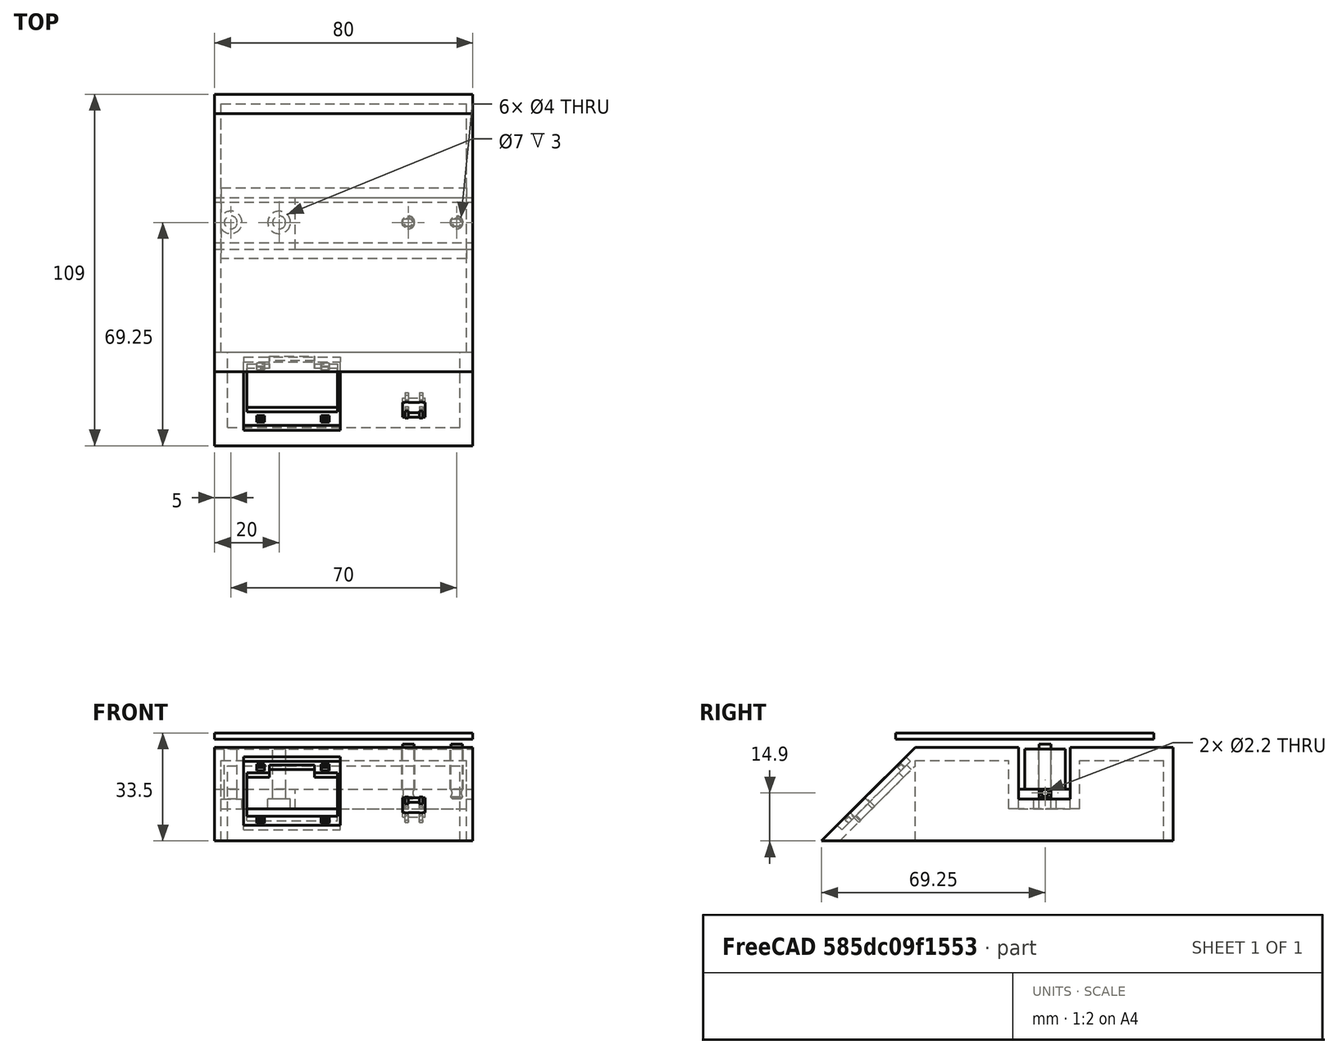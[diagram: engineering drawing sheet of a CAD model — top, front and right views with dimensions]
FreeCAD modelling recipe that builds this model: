
FCSTD DOCUMENT  (FreeCAD 0.19R24291 (Git))
Label: Scale
License: All rights reserved
LicenseURL: http://en.wikipedia.org/wiki/All_rights_reserved
objects: Part::Box×19, Part::Cylinder×11, Part::Cut×5, Part::MultiFuse×4, Part::Compound×3, Part::FeaturePython×3, Part::Chamfer×2, Mesh::Feature×1, Part::Thickness×1, Part::MultiCommon×1
note: 49 computed .brp shape members not serialized (recipe doc carries the construction recipe); baked Part::Feature solids carry a one-line shape summary decoded from their .brp

FEATURE [Part::Box] Box  label="Eje001"
  AttacherType = Attacher::AttachEngine3D
  Height = 12.5
  Length = 80
  Width = 12.5
FEATURE [Part::Cylinder] Cylinder
  Angle = 360
  AttacherType = Attacher::AttachEngine3D
  AttachmentOffset = pos=(5,6.25,-12.5) rot=(0,0,1;0rad)
  Height = 13
  MapMode = 5
  Placement = pos=(5,6.25,0) rot=(0,0,1;0rad)
  Radius = 2
  Support = -> [Box]
  expr: .AttachmentOffset.Base.y = Box.Width / 2
  expr: .AttachmentOffset.Base.z = -Box.Height
FEATURE [Part::Cylinder] Cylinder001
  Angle = 360
  AttacherType = Attacher::AttachEngine3D
  AttachmentOffset = pos=(20,6.25,-12.5) rot=(0,0,1;0rad)
  Height = 13
  MapMode = 5
  Placement = pos=(20,6.25,0) rot=(0,0,1;0rad)
  Radius = 2
  Support = -> [Box]
  expr: .AttachmentOffset.Base.y = Box.Width / 2
  expr: .AttachmentOffset.Base.z = -Box.Height
FEATURE [Part::Cylinder] Cylinder002
  Angle = 360
  AttacherType = Attacher::AttachEngine3D
  AttachmentOffset = pos=(75,6.25,-12.5) rot=(0,0,1;0rad)
  Height = 13
  MapMode = 5
  Placement = pos=(75,6.25,0) rot=(0,0,1;0rad)
  Radius = 2
  Support = -> [Box]
  expr: .AttachmentOffset.Base.y = Box.Width / 2
  expr: .AttachmentOffset.Base.z = -Box.Height
  expr: .AttachmentOffset.Base.x = Box.Length - 5mm
FEATURE [Part::Cylinder] Cylinder003
  Angle = 360
  AttacherType = Attacher::AttachEngine3D
  AttachmentOffset = pos=(60,6.25,-12.5) rot=(0,0,1;0rad)
  Height = 13
  MapMode = 5
  Placement = pos=(60,6.25,0) rot=(0,0,1;0rad)
  Radius = 2
  Support = -> [Box]
  expr: .AttachmentOffset.Base.y = Box.Width / 2
  expr: .AttachmentOffset.Base.z = -Box.Height
  expr: .AttachmentOffset.Base.x = Box.Length - 20mm
FEATURE [Part::Compound] Compound  label="AgujerosEje"
  Links = -> [Cylinder,Cylinder001,Cylinder002,Cylinder003]
FEATURE [Part::Cut] Cut  label="Eje"
  Base = -> Box
  Tool = -> Compound
FEATURE [Part::Cylinder] Cylinder004
  Angle = 360
  AttacherType = Attacher::AttachEngine3D
  AttachmentOffset = pos=(75,6.25,-12.5) rot=(0,0,1;0rad)
  Height = 17
  Placement = pos=(75,6.25,-3) rot=(0,0,1;0rad)
  Radius = 1.8
  Support = -> [Box]
  expr: .AttachmentOffset.Base.y = Box.Width / 2
  expr: .AttachmentOffset.Base.z = -Box.Height
  expr: .AttachmentOffset.Base.x = Box.Length - 5mm
FEATURE [Part::Cylinder] Cylinder005
  Angle = 360
  AttacherType = Attacher::AttachEngine3D
  AttachmentOffset = pos=(60,6.25,-12.5) rot=(0,0,1;0rad)
  Height = 17
  Placement = pos=(60,6.25,-3) rot=(0,0,1;0rad)
  Radius = 1.8
  Support = -> [Box]
  expr: .AttachmentOffset.Base.y = Box.Width / 2
  expr: .AttachmentOffset.Base.z = -Box.Height
  expr: .AttachmentOffset.Base.x = Box.Length - 20mm
FEATURE [Part::Compound] Compound001  label="PernosPlato001"
  Links = -> [Cylinder005,Cylinder004]
FEATURE [Part::Chamfer] Chamfer  label="PernosPlato002"
  Base = -> Compound001
  Edges = 2 edges r=0.5: [Edge3,Edge6]
FEATURE [Part::Cylinder] Cylinder006  label="OrificioTransversalPernos"
  Angle = 360
  AttacherType = Attacher::AttachEngine3D
  Height = 25
  Placement = pos=(55,6.25,-1.1) rot=(0,1,0;1.5708rad)
  Radius = 1.1
  expr: .Placement.Base.y = Box.Width / 2
  expr: .Placement.Base.x = Box.Length - Height
  expr: .Placement.Base.z = -Radius
FEATURE [Part::Cut] Cut001  label="PernosPlato"
  Base = -> Chamfer
  Tool = -> Cylinder006
FEATURE [Part::Box] Box001  label="Plato001"
  AttacherType = Attacher::AttachEngine3D
  Height = 2
  Length = 80
  Placement = pos=(0,-40,15.5) rot=(0,0,1;0rad)
  Width = 80
  expr: Length = <<Eje001>>.Length
  expr: Width = <<Eje001>>.Length
  expr: .Placement.Base.y = -Width / 2
  expr: .Placement.Base.z = <<Eje001>>.Height + 3mm
FEATURE [Part::Box] Box002  label="Soporte001"
  AttacherType = Attacher::AttachEngine3D
  Height = 6
  Length = 25
  Placement = pos=(0,-2,-6) rot=(0,0,1;0rad)
  Width = 16
FEATURE [Part::Compound] Compound003  label="Plato MAL"
  Links = -> [Box001,Cut001]
FEATURE [Mesh::Feature] BasculaPlato  label="Plato STL"
FEATURE [Part::Cylinder] Cylinder007
  Angle = 360
  AttacherType = Attacher::AttachEngine3D
  AttachmentOffset = pos=(20,6.25,-12.5) rot=(0,0,1;0rad)
  Height = 20
  MapMode = 5
  Placement = pos=(20,6.25,0) rot=(0,0,1;0rad)
  Radius = 2
  Support = -> [Box]
  expr: .AttachmentOffset.Base.y = Box.Width / 2
  expr: .AttachmentOffset.Base.z = -Box.Height
FEATURE [Part::Cylinder] Cylinder008
  Angle = 360
  AttacherType = Attacher::AttachEngine3D
  AttachmentOffset = pos=(5,6.25,-12.5) rot=(0,0,1;0rad)
  Height = 20
  MapMode = 5
  Placement = pos=(5,6.25,0) rot=(0,0,1;0rad)
  Radius = 2
  Support = -> [Box]
  expr: .AttachmentOffset.Base.y = Box.Width / 2
  expr: .AttachmentOffset.Base.z = -Box.Height
FEATURE [Part::Cylinder] Cylinder009
  Angle = 360
  AttacherType = Attacher::AttachEngine3D
  AttachmentOffset = pos=(5,6.25,-15.5) rot=(0,0,1;0rad)
  Height = 6
  MapMode = 5
  Placement = pos=(5,6.25,-3) rot=(0,0,1;0rad)
  Radius = 3.5
  Support = -> [Box]
  expr: .AttachmentOffset.Base.y = Box.Width / 2
  expr: .AttachmentOffset.Base.z = -Box.Height - 3mm
FEATURE [Part::Cylinder] Cylinder010
  Angle = 360
  AttacherType = Attacher::AttachEngine3D
  AttachmentOffset = pos=(20,6.25,-15.5) rot=(0,0,1;0rad)
  Height = 6
  MapMode = 5
  Placement = pos=(20,6.25,-3) rot=(0,0,1;0rad)
  Radius = 3.5
  Support = -> [Box]
  expr: .AttachmentOffset.Base.y = Box.Width / 2
  expr: .AttachmentOffset.Base.z = -Box.Height - 3mm
FEATURE [Part::MultiFuse] Fusion
  Placement = pos=(0,0,-6) rot=(0,0,1;0rad)
  Shapes = -> [Cylinder008,Cylinder007,Cylinder009,Cylinder010]
FEATURE [Part::Cut] Cut002
  Base = -> Box002
  Tool = -> Fusion
FEATURE [Part::Box] Box003  label="Soporte002"
  AttacherType = Attacher::AttachEngine3D
  Height = 4
  Length = 80
  Placement = pos=(0,-34,9) rot=(0,0,1;0rad)
  Width = 32
FEATURE [Part::Box] Box004  label="Soporte003"
  AttacherType = Attacher::AttachEngine3D
  Height = 4
  Length = 80
  Placement = pos=(0,14,9) rot=(0,0,1;0rad)
  Width = 32
FEATURE [Part::Box] Box005  label="Soporte004"
  AttacherType = Attacher::AttachEngine3D
  Height = 18
  Length = 80
  Placement = pos=(0,-5,-6) rot=(0,0,1;0rad)
  Width = 3
FEATURE [Part::Box] Box006  label="Soporte005"
  AttacherType = Attacher::AttachEngine3D
  Height = 18
  Length = 80
  Placement = pos=(0,14,-6) rot=(0,0,1;0rad)
  Width = 3
FEATURE [Part::Box] Box008  label="Fondo001"
  AttacherType = Attacher::AttachEngine3D
  Height = 25
  Length = 80
  Placement = pos=(0,43,-16) rot=(0,0,1;0rad)
  Width = 3
FEATURE [Part::Box] Box009  label="TapaIzquierda"
  AttacherType = Attacher::AttachEngine3D
  Height = 25
  Length = 80
  Placement = pos=(2,-34,-16) rot=(0,0,1;1.5708rad)
  Width = 2
FEATURE [Part::Box] Box010  label="TapaDerecha"
  AttacherType = Attacher::AttachEngine3D
  Height = 25
  Length = 80
  Placement = pos=(80,-34,-16) rot=(0,0,1;1.5708rad)
  Width = 2
FEATURE [Part::Box] Box011  label="AgujeroEje"
  AttacherType = Attacher::AttachEngine3D
  Height = 12.5
  Length = 80
  Placement = pos=(0,-2,-3) rot=(0,0,1;0rad)
  Width = 16
FEATURE [Part::MultiFuse] Fusion001  label="TapasLaterales"
  Shapes = -> [Box009,Box010]
FEATURE [Part::Cut] Cut003  label="TapasLateralesCompletas"
  Base = -> Fusion001
  Tool = -> Box011
FEATURE [Part::Box] Box013  label="FrenteLimite"
  AttacherType = Attacher::AttachEngine3D
  Height = 29
  Length = 80
  Placement = pos=(0,-65,-16) rot=(0,0,1;0rad)
  Width = 31
FEATURE [Part::Box] Box014  label="Frente003"
  AttacherType = Attacher::AttachEngine3D
  Height = 49.77
  Length = 80
  Placement = pos=(0,-69.1924,-22.1924) rot=(-1,0,0;0.785398rad)
  Width = 27
FEATURE [Part::Thickness] Thickness  label="FrenteAngulo"
  Faces = -> Box014 [Face4,Face6,Face5]
  Intersection = true
  Join = 2
  Mode = 0
  SelfIntersection = true
  Value = -4
FEATURE [Part::MultiCommon] Common  label="Frente"
  Refine = true
  Shapes = -> [Thickness,Box013]
FEATURE [Part::Box] Box015  label="Pinhole"
  AttacherType = Attacher::AttachEngine3D
  Height = 10
  Length = 1
  Width = 1
FEATURE [Part::FeaturePython] Array  label="BotónAgujeros"  # Draft array (typed FeaturePython)
  Angle = 360
  ArrayType = 0
  Axis = (0,0,1)
  Base = -> Box015
  Center = (0,0,0)
  Fuse = false
  IntervalAxis = (0,0,0)
  IntervalX = (4.5,0,0)
  IntervalY = (0,6,0)
  IntervalZ = (0,0,1)
  NumberPolar = 1
  NumberX = 2
  NumberY = 2
  NumberZ = 1
  Placement = pos=(59,-50.8567,-10.8374) rot=(1,0,0;0.785398rad)
FEATURE [Part::Box] Box016  label="Pinhole001"
  AttacherType = Attacher::AttachEngine3D
  Height = 2
  Length = 2.5
  Placement = pos=(-47,-4,5) rot=(0,0,1;0rad)
  Width = 1.6
FEATURE [Part::Chamfer] Chamfer001  label="PinholeSuave"
  Base = -> Box016
  Edges = 8 edges r=0.1: [Edge1,Edge2,Edge3,Edge5,Edge6,Edge7,Edge10,Edge12]
FEATURE [Part::FeaturePython] Array001  label="PitorrosPantalla"  # Draft array (typed FeaturePython)
  Angle = 360
  ArrayType = 0
  Axis = (0,0,1)
  Base = -> Chamfer001
  Center = (0,0,0)
  Fuse = false
  IntervalAxis = (0,0,0)
  IntervalX = (20,0,0)
  IntervalY = (0,23,0)
  IntervalZ = (0,0,1)
  NumberPolar = 1
  NumberX = 2
  NumberY = 2
  NumberZ = 1
FEATURE [Part::Box] Box017  label="HuecoPantalla"
  AttacherType = Attacher::AttachEngine3D
  AttachmentOffset = pos=(9,-49,-2) rot=(0,0,1;0rad)
  Height = 2
  Length = 30
  MapMode = 5
  Placement = pos=(9,-56.734,-12.5624) rot=(1,0,0;0.785398rad)
  Support = -> [Common]
  Width = 30
FEATURE [Part::MultiFuse] Fusion003  label="PitorrosPantalla001"
  Placement = pos=(60,-48,-11.59) rot=(1,0,0;0.785398rad)
  Refine = true
  Shapes = -> [Array001]
FEATURE [Part::Box] Box018  label="AgujeroCablePantalla"
  AttacherType = Attacher::AttachEngine3D
  AttachmentOffset = pos=(17,-24.5,-4) rot=(0,0,1;0rad)
  Height = 10
  Length = 14
  MapMode = 5
  Placement = pos=(17,-37.9957,3.34746) rot=(1,0,0;0.785398rad)
  Support = -> [Thickness]
  Width = 4
FEATURE [Part::Box] Box019  label="HuecoPantalla001"
  AttacherType = Attacher::AttachEngine3D
  AttachmentOffset = pos=(10,-43,-5) rot=(0,0,1;0rad)
  Height = 5
  Length = 28
  MapMode = 5
  Placement = pos=(10,-50.3701,-10.4411) rot=(1,0,0;0.785398rad)
  Support = -> [Common]
  Width = 19
FEATURE [Part::Box] Box020  label="HuecoBoton"
  AttacherType = Attacher::AttachEngine3D
  AttachmentOffset = pos=(58.25,-43.4,-2) rot=(0,0,1;0rad)
  Height = 2
  Length = 7
  MapMode = 5
  Placement = pos=(58.25,-52.7742,-8.60265) rot=(1,0,0;0.785398rad)
  Support = -> [Common]
  Width = 6.5
FEATURE [Part::MultiFuse] Fusion002  label="agujerosFrente"
  Refine = true
  Shapes = -> [Array,Box017,Box018,Box019,Box020]
FEATURE [Part::Cut] Cut005  label="FrentePerforado"
  Base = -> Common
  Refine = true
  Tool = -> Fusion002
FEATURE [Part::FeaturePython] Connect  label="Cuerpo"  # WARN: FeaturePython — macro-defined, semantics opaque (R4)
  Objects = -> [Cut002,Box003,Box004,Box005,Box006,Box008,Cut003,Cut005,Fusion003]
  Refine = true
  Tolerance = 0
